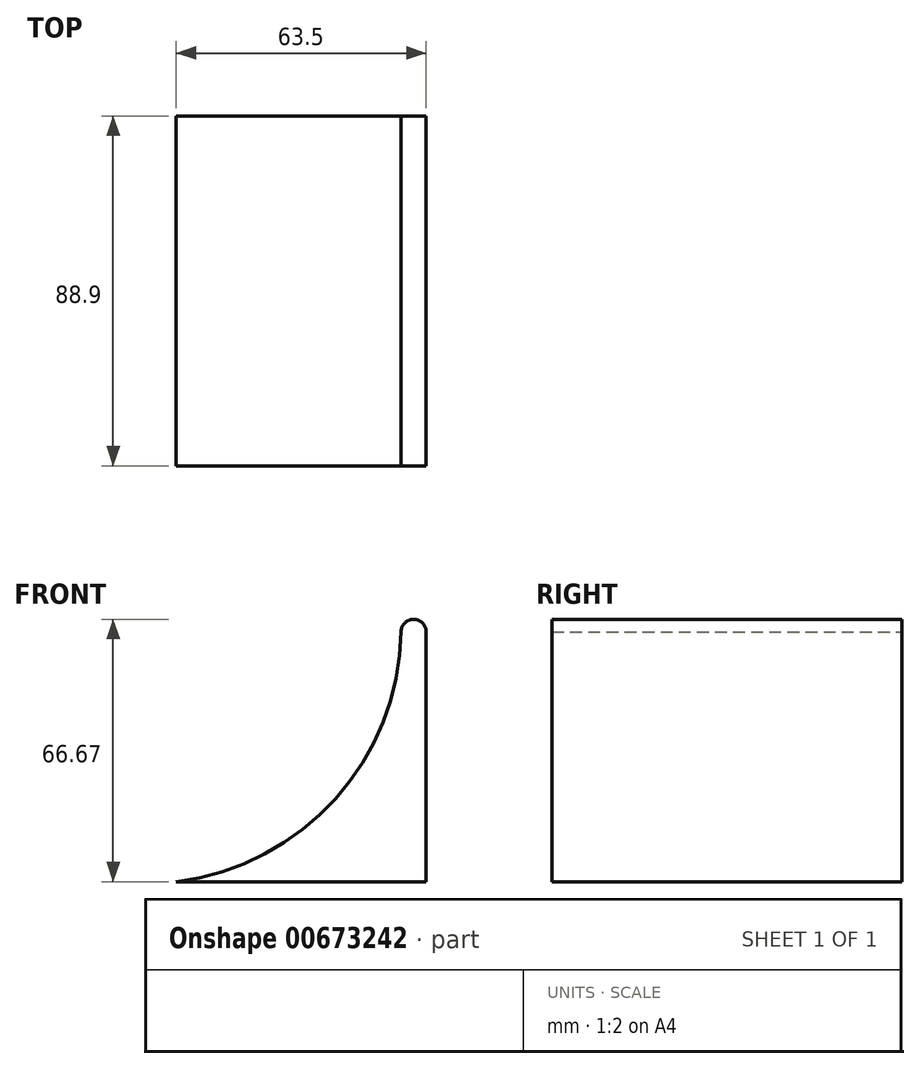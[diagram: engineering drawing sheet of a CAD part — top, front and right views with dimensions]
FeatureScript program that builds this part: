
annotation { "Feature Type Name" : "Feature", "Feature Type Description" : "" }
export const myFeature = defineFeature(function(context is Context, id is Id, definition is map)
    precondition{}
    {
        {
            var Q0;
            Q0=qCreatedBy(makeId("Front.planeOp"),FACE);
            var sketch = newSketch(context, id + "F0", { "sketchPlane" : qUnion([Q0])});
            skLineSegment(sketch, "E0", {"start": v(0, 0) * mm, "end": v(-63.5, 0) * mm});
            skLineSegment(sketch, "E1", {"start": v(0, 0) * mm, "end": v(0, 63.5) * mm});
            skArc(sketch, "E2", {"start": v(0, 63.5) * mm, "mid": v(-3.18, 66.67) * mm, "end": v(-6.35, 63.5) * mm});
            skArc(sketch, "E3", {"start": v(-63.5, 0) * mm, "mid": v(-23.04, 21.05) * mm, "end": v(-6.35, 63.5) * mm});
            skLineSegment(sketch, "E4", {"start": v(0, 63.5) * mm, "end": v(0, 63.5) * mm});
            skSolve(sketch);
        }
        {
            var Q0;
            Q0 = qSketchRegion(id + "F0", true);
            extrude(context, id + "F1", {"entities" : qUnion([Q0]), "endBound" : BoundingType.SYMMETRIC, "depth" : 88.9 * mm, "offsetDistance" : 25.4 * mm});
        }
    });
